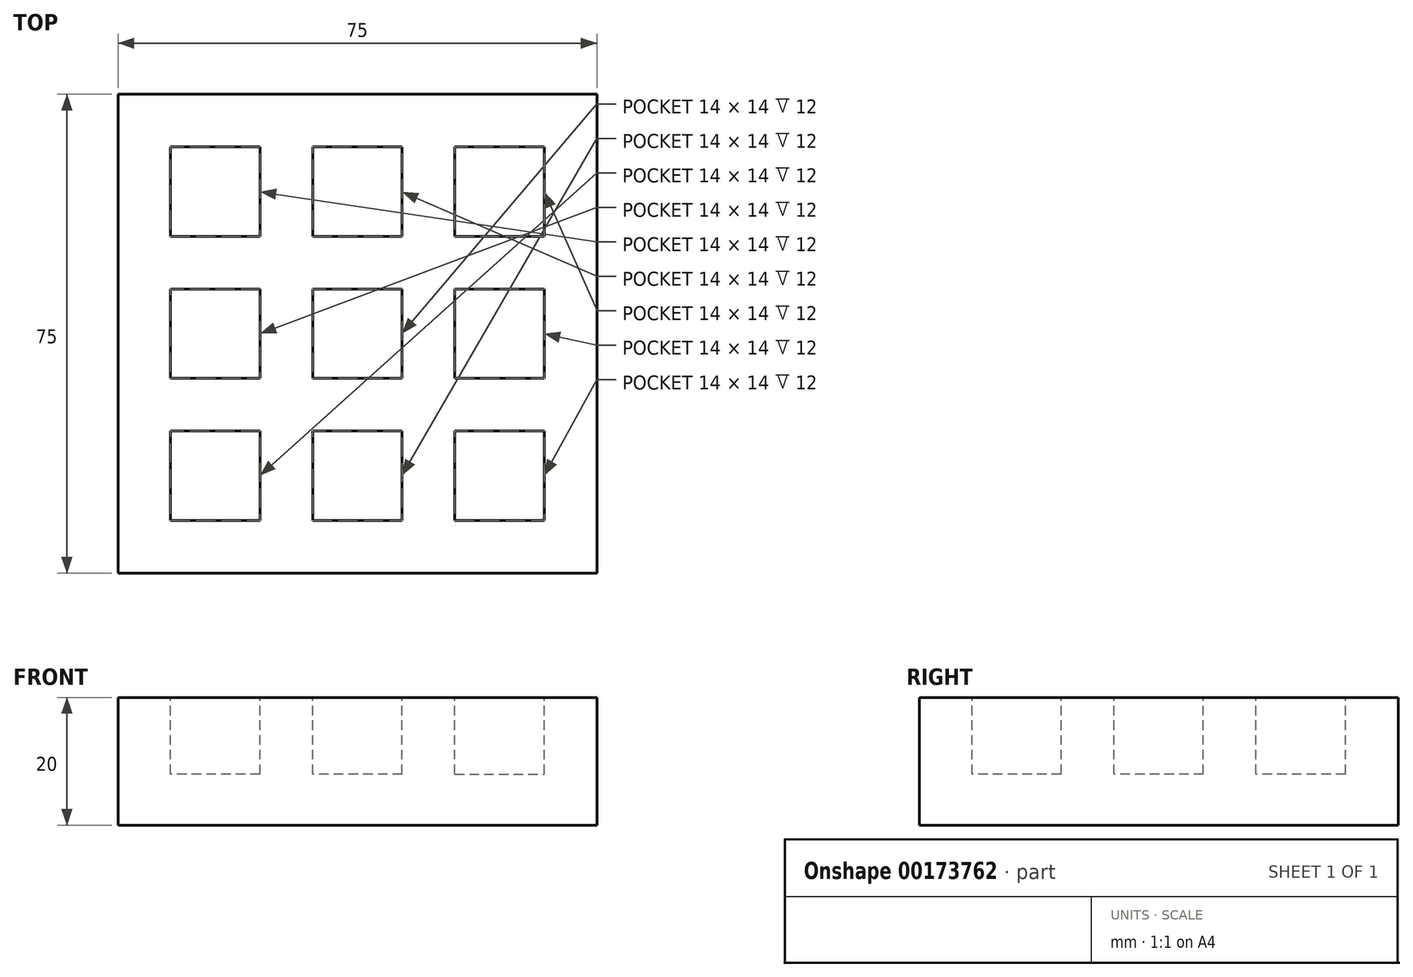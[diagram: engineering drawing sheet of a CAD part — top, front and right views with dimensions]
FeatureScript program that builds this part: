
annotation { "Feature Type Name" : "Feature", "Feature Type Description" : "" }
export const myFeature = defineFeature(function(context is Context, id is Id, definition is map)
    precondition{}
    {
        {
            var Q0;
            Q0=qCreatedBy(makeId("Top.planeOp"),FACE);
            var sketch = newSketch(context, id + "F0", { "sketchPlane" : qUnion([Q0])});
            skLineSegment(sketch, "E0.bottom", {"start": v(37.5, 37.5) * mm, "end": v(-37.5, 37.5) * mm});
            skLineSegment(sketch, "E0.top", {"start": v(37.5, -37.5) * mm, "end": v(-37.5, -37.5) * mm});
            skLineSegment(sketch, "E0.left", {"start": v(37.5, 37.5) * mm, "end": v(37.5, -37.5) * mm});
            skLineSegment(sketch, "E0.right", {"start": v(-37.5, 37.5) * mm, "end": v(-37.5, -37.5) * mm});
            skPoint(sketch, "E0.middle", {"position": v(0, 0) * mm});
            skSolve(sketch);
        }
        {
            var Q0;
            Q0=makeQuery(id+"F0.imprint","IMPRINT",FACE,{"disambiguationData":[TD([[makeQuery(id+"F0.imprint","IMPRINT",EDGE,{"derivedFrom":sQuery(id+"F0.wireOp",EDGE,"E0.bottom")}),1.0]])]});
            extrude(context, id + "F1", {"entities" : qUnion([Q0]), "depth" : 20 * mm});
        }
        {
            var Q0;
            Q0=makeQuery(id+"F1.opExtrude","CAP_FACE",FACE,{"disambiguationData":[OSD([sQuery(id+"F0.wireOp",EDGE,"E0.bottom"),sQuery(id+"F0.wireOp",EDGE,"E0.top"),sQuery(id+"F0.wireOp",EDGE,"E0.left"),sQuery(id+"F0.wireOp",EDGE,"E0.right")])],"isStart":false});
            var sketch = newSketch(context, id + "F2", { "sketchPlane" : qUnion([Q0])});
            skLineSegment(sketch, "E1.bottom", {"start": v(7, 7) * mm, "end": v(-7, 7) * mm});
            skLineSegment(sketch, "E1.top", {"start": v(7, -7) * mm, "end": v(-7, -7) * mm});
            skLineSegment(sketch, "E1.left", {"start": v(7, 7) * mm, "end": v(7, -7) * mm});
            skLineSegment(sketch, "E1.right", {"start": v(-7, 7) * mm, "end": v(-7, -7) * mm});
            skPoint(sketch, "E1.middle", {"position": v(0, 0) * mm});
            skLineSegment(sketch, "E2.bottom", {"start": v(7, 15.25) * mm, "end": v(-7, 15.25) * mm});
            skLineSegment(sketch, "E2.top", {"start": v(7, 29.25) * mm, "end": v(-7, 29.25) * mm});
            skLineSegment(sketch, "E2.left", {"start": v(7, 15.25) * mm, "end": v(7, 29.25) * mm});
            skLineSegment(sketch, "E2.right", {"start": v(-7, 15.25) * mm, "end": v(-7, 29.25) * mm});
            skPoint(sketch, "E2.middle", {"position": v(0, 22.25) * mm});
            skLineSegment(sketch, "E3.bottom", {"start": v(15.25, 7) * mm, "end": v(29.25, 7) * mm});
            skLineSegment(sketch, "E3.top", {"start": v(15.25, -7) * mm, "end": v(29.25, -7) * mm});
            skLineSegment(sketch, "E3.left", {"start": v(15.25, 7) * mm, "end": v(15.25, -7) * mm});
            skLineSegment(sketch, "E3.right", {"start": v(29.25, 7) * mm, "end": v(29.25, -7) * mm});
            skPoint(sketch, "E3.middle", {"position": v(22.25, 0) * mm});
            skLineSegment(sketch, "E4.bottom", {"start": v(15.25, -15.25) * mm, "end": v(29.25, -15.25) * mm});
            skLineSegment(sketch, "E4.top", {"start": v(15.25, -29.25) * mm, "end": v(29.25, -29.25) * mm});
            skLineSegment(sketch, "E4.left", {"start": v(15.25, -15.25) * mm, "end": v(15.25, -29.25) * mm});
            skLineSegment(sketch, "E4.right", {"start": v(29.25, -15.25) * mm, "end": v(29.25, -29.25) * mm});
            skPoint(sketch, "E4.middle", {"position": v(22.25, -22.25) * mm});
            skLineSegment(sketch, "E5.bottom", {"start": v(7, -15.25) * mm, "end": v(-7, -15.25) * mm});
            skLineSegment(sketch, "E5.top", {"start": v(7, -29.25) * mm, "end": v(-7, -29.25) * mm});
            skLineSegment(sketch, "E5.left", {"start": v(7, -15.25) * mm, "end": v(7, -29.25) * mm});
            skLineSegment(sketch, "E5.right", {"start": v(-7, -15.25) * mm, "end": v(-7, -29.25) * mm});
            skPoint(sketch, "E5.middle", {"position": v(0, -22.25) * mm});
            skLineSegment(sketch, "E6.bottom", {"start": v(-15.25, 7) * mm, "end": v(-29.25, 7) * mm});
            skLineSegment(sketch, "E6.top", {"start": v(-15.25, -7) * mm, "end": v(-29.25, -7) * mm});
            skLineSegment(sketch, "E6.left", {"start": v(-15.25, 7) * mm, "end": v(-15.25, -7) * mm});
            skLineSegment(sketch, "E6.right", {"start": v(-29.25, 7) * mm, "end": v(-29.25, -7) * mm});
            skPoint(sketch, "E6.middle", {"position": v(-22.25, 0) * mm});
            skLineSegment(sketch, "E7.bottom", {"start": v(-29.25, 29.25) * mm, "end": v(-15.25, 29.25) * mm});
            skLineSegment(sketch, "E7.top", {"start": v(-29.25, 15.25) * mm, "end": v(-15.25, 15.25) * mm});
            skLineSegment(sketch, "E7.left", {"start": v(-29.25, 29.25) * mm, "end": v(-29.25, 15.25) * mm});
            skLineSegment(sketch, "E7.right", {"start": v(-15.25, 29.25) * mm, "end": v(-15.25, 15.25) * mm});
            skPoint(sketch, "E7.middle", {"position": v(-22.25, 22.25) * mm});
            skPoint(sketch, "E7.middle.positionSnap0", {"position": v(-22.25, 7) * mm});
            skPoint(sketch, "E7.middle.positionSnap1", {"position": v(-7, 22.25) * mm});
            skPoint(sketch, "E7.centerSnap0", {"position": v(-22.25, 7) * mm});
            skPoint(sketch, "E7.centerSnap1", {"position": v(-7, 22.25) * mm});
            skLineSegment(sketch, "E8.bottom", {"start": v(-15.25, -15.25) * mm, "end": v(-29.25, -15.25) * mm});
            skLineSegment(sketch, "E8.top", {"start": v(-15.25, -29.25) * mm, "end": v(-29.25, -29.25) * mm});
            skLineSegment(sketch, "E8.left", {"start": v(-15.25, -15.25) * mm, "end": v(-15.25, -29.25) * mm});
            skLineSegment(sketch, "E8.right", {"start": v(-29.25, -15.25) * mm, "end": v(-29.25, -29.25) * mm});
            skPoint(sketch, "E8.middle", {"position": v(-22.25, -22.25) * mm});
            skPoint(sketch, "E8.middle.positionSnap0", {"position": v(-7, -22.25) * mm});
            skPoint(sketch, "E8.middle.positionSnap1", {"position": v(-22.25, -7) * mm});
            skPoint(sketch, "E8.centerSnap0", {"position": v(-7, -22.25) * mm});
            skPoint(sketch, "E8.centerSnap1", {"position": v(-22.25, -7) * mm});
            skLineSegment(sketch, "E9.bottom", {"start": v(15.25, 15.25) * mm, "end": v(29.25, 15.25) * mm});
            skLineSegment(sketch, "E9.top", {"start": v(15.25, 29.25) * mm, "end": v(29.25, 29.25) * mm});
            skLineSegment(sketch, "E9.left", {"start": v(15.25, 15.25) * mm, "end": v(15.25, 29.25) * mm});
            skLineSegment(sketch, "E9.right", {"start": v(29.25, 15.25) * mm, "end": v(29.25, 29.25) * mm});
            skPoint(sketch, "E9.middle", {"position": v(22.25, 22.25) * mm});
            skPoint(sketch, "E9.middle.positionSnap0", {"position": v(22.25, 7) * mm});
            skPoint(sketch, "E9.middle.positionSnap1", {"position": v(7, 22.25) * mm});
            skPoint(sketch, "E9.centerSnap0", {"position": v(22.25, 7) * mm});
            skPoint(sketch, "E9.centerSnap1", {"position": v(7, 22.25) * mm});
            skLineSegment(sketch, "E10", {"start": v(-15.25, 15.25) * mm, "end": v(-7, 7) * mm});
            skLineSegment(sketch, "E11", {"start": v(15.25, -15.25) * mm, "end": v(7, -7) * mm});
            skLineSegment(sketch, "E12", {"start": v(-7, -7) * mm, "end": v(-15.25, -15.25) * mm});
            skSolve(sketch);
        }
        {
            var Q0;
            Q0=makeQuery(id+"F2.imprint","IMPRINT",FACE,{"disambiguationData":[TD([[makeQuery(id+"F2.imprint","IMPRINT",EDGE,{"derivedFrom":sQuery(id+"F2.wireOp",EDGE,"E1.bottom")}),1.0]])]});
            var Q1;
            Q1=makeQuery(id+"F2.imprint","IMPRINT",FACE,{"disambiguationData":[TD([[makeQuery(id+"F2.imprint","IMPRINT",EDGE,{"derivedFrom":sQuery(id+"F2.wireOp",EDGE,"E4.bottom")}),-1.0]])]});
            var Q2;
            Q2=makeQuery(id+"F2.imprint","IMPRINT",FACE,{"disambiguationData":[TD([[makeQuery(id+"F2.imprint","IMPRINT",EDGE,{"derivedFrom":sQuery(id+"F2.wireOp",EDGE,"E3.bottom")}),-1.0]])]});
            var Q3;
            Q3=makeQuery(id+"F2.imprint","IMPRINT",FACE,{"disambiguationData":[TD([[makeQuery(id+"F2.imprint","IMPRINT",EDGE,{"derivedFrom":sQuery(id+"F2.wireOp",EDGE,"E9.bottom")}),1.0]])]});
            var Q4;
            Q4=makeQuery(id+"F2.imprint","IMPRINT",FACE,{"disambiguationData":[TD([[makeQuery(id+"F2.imprint","IMPRINT",EDGE,{"derivedFrom":sQuery(id+"F2.wireOp",EDGE,"E2.bottom")}),-1.0]])]});
            var Q5;
            Q5=makeQuery(id+"F2.imprint","IMPRINT",FACE,{"disambiguationData":[TD([[makeQuery(id+"F2.imprint","IMPRINT",EDGE,{"derivedFrom":sQuery(id+"F2.wireOp",EDGE,"E7.bottom")}),-1.0]])]});
            var Q6;
            Q6=makeQuery(id+"F2.imprint","IMPRINT",FACE,{"disambiguationData":[TD([[makeQuery(id+"F2.imprint","IMPRINT",EDGE,{"derivedFrom":sQuery(id+"F2.wireOp",EDGE,"E6.bottom")}),1.0]])]});
            var Q7;
            Q7=makeQuery(id+"F2.imprint","IMPRINT",FACE,{"disambiguationData":[TD([[makeQuery(id+"F2.imprint","IMPRINT",EDGE,{"derivedFrom":sQuery(id+"F2.wireOp",EDGE,"E8.bottom")}),1.0]])]});
            var Q8;
            Q8=makeQuery(id+"F2.imprint","IMPRINT",FACE,{"disambiguationData":[TD([[makeQuery(id+"F2.imprint","IMPRINT",EDGE,{"derivedFrom":sQuery(id+"F2.wireOp",EDGE,"E5.bottom")}),1.0]])]});
            extrude(context, id + "F3", {"entities" : qUnion([Q0, Q1, Q2, Q3, Q4, Q5, Q6, Q7, Q8]), "operationType" : NewBodyOperationType.REMOVE, "oppositeDirection" : true, "depth" : 12 * mm});
        }
    });
